# Revit family: Vitra-Built-inBath&ShowerMixer(Exposedpart)-BravaSeries-A42394
name_source: partatom
category: Plumbing Fixtures
revit_build: Autodesk Revit 2017 (Build: 20160225_1515(x64)
units: mm (PartAtom-declared; Revit-internal decimal feet)

## family parameters
Cut with Voids When Loaded = No
Host = Face
OmniClass Number = 23.45.55.17
OmniClass Title = Mixing Faucets
Part Type = Normal
Room Calculation Point = No
Round Connector Dimension = Use Diameter
Shared = Yes

## types (1)
- Bath&ShowerMixer(Built-in)-Vitra-AxeS Series-A42394
    Article No. (default) = A42394
    BIMobject category = Bath/Shower Mixer
    CW Connection = Yes
    CWFU = 0
    Coating Material = Vitra-Chrome
    Color = Chrome
    Connection Diameter (mm) = 15 mm  [stored 0.0492126 ft]
    Cost = 0 $
    Default Elevation = 850 mm  [stored 2.78871 ft]
    Depth(mm) = 198 mm
    Description = Built-in Basin Mixer (Exposed Part)
    Design country = Turkey
    Flow Rate(L/min. - 3 bar) = 5
    HW Connection = Yes
    HWFU = 0
    Height(mm) = 145 mm
    Hot Water Supply (max.) = 80 °C
    Hot Water temperature, factory set to = 38 °C
    IFC Classification = Sanitary Terminal
    Main Material = Brass
    Manufacturer = Vitra
    Manufacturer name = Vitra
    Masterformat 2014 Code = 22 40 00
    Masterformat 2014 Description = Plumbing Fixtures
    Min. flow pressure of = 0.5 bar
    Model = A42394
    MountingType = Wall-mounted (exposed part)
    NBS Referans Code = 45-35-70/315
    NBS Referans Description = Water supply fittings for baths
    Nominal height = 0.000
    Nominal width = 0.000
    Number Of Connections = 1 mm  [stored 0.00328084 ft]
    OmniClass Code = 23.45.55.17
    OmniClass Description = Mixing Faucets
    Product SKU = A42394
    Product Type = Built-in bath/shower mixer (exposed part)
    Product certification = https://vitraglobal.com
    Product data url = https://www.vitra.com.tr
    Product family = Brava
    Product group = Bath&Shower Mixer (exposed part)
    Range of Hot Water Supply = 5 - 65 °C
    Range of flow pressure = 1 - 5 bar
    Technical description = https://www.vitra.com.tr
    Test Pressure = 16 bar
    UNSPSC Code = 301815
    URL = https://vitraglobal.com
    Uniclass 1.4 Code = L725111
    Uniclass 1.4 Description = Mixer taps
    Uniclass 2.0 Code = Pr_40_20_87_09
    Uniclass 2.0 Description = Bath taps
    Uniclass 2015 Code = Pr_40_20_87_09
    Uniclass 2015 Name = Bath taps
    Uniformat II Code = 22 40 00
    Uniformat II Description = Plumbing Fixture
    WFU = 0
    Warranty Period (Year) = 10 Years
    Weight Net (kg) = 2.220
    Width(mm) = 200 mm
    Youtube = https://www.youtube.com

note: [stored X ft] marks values corroborated as IEEE doubles in the binary element streams (Revit-internal decimal feet)

## geometry (parser evidence)
native form markers: Sweep x3
no freeform markers — native parametric forms only
